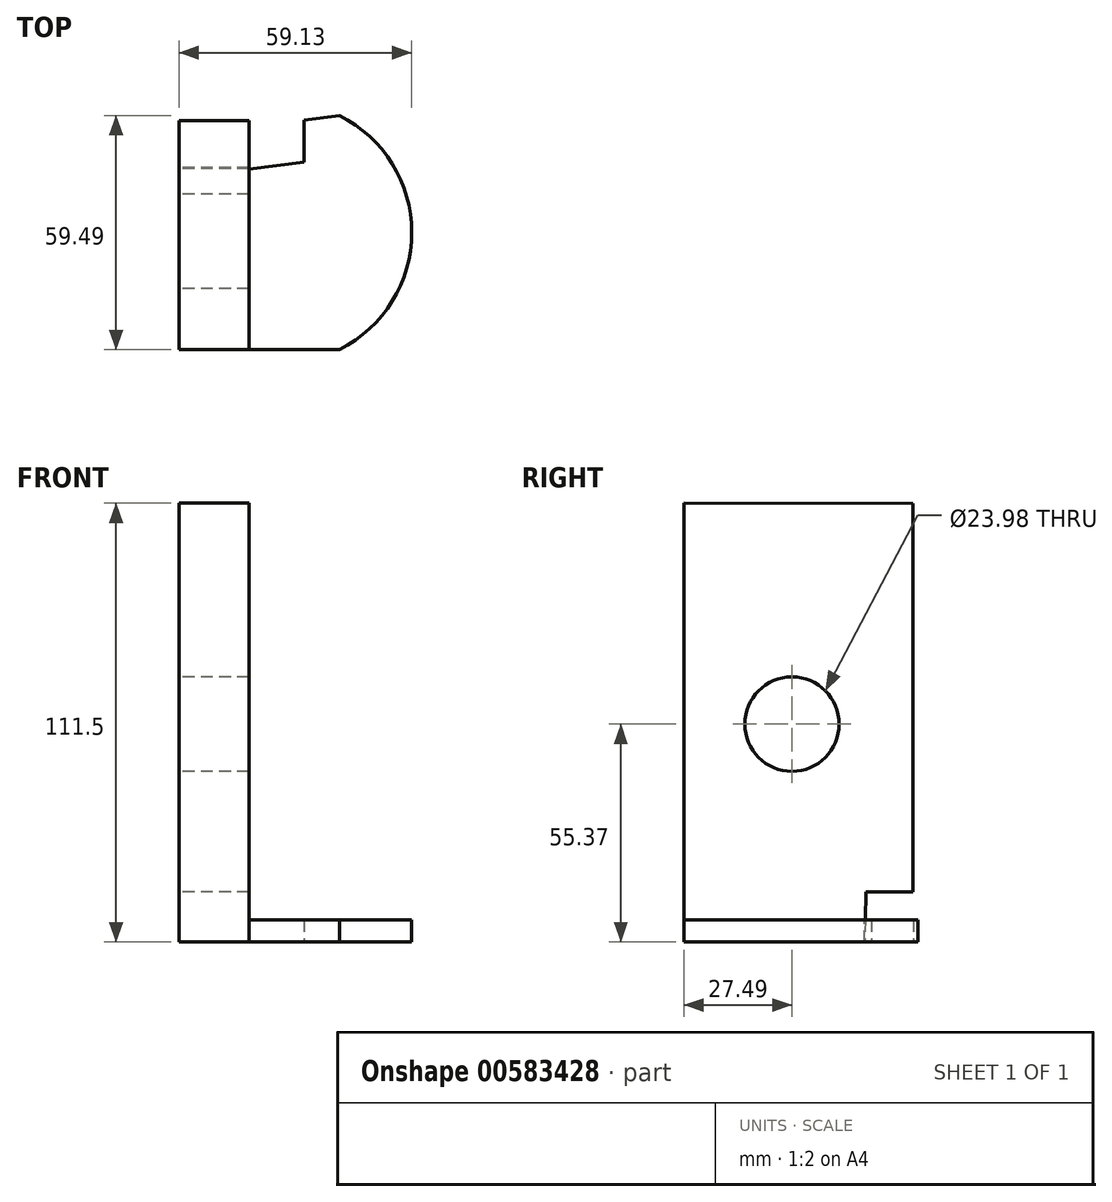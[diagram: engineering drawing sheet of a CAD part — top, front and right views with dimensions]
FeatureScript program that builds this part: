
annotation { "Feature Type Name" : "Feature", "Feature Type Description" : "" }
export const myFeature = defineFeature(function(context is Context, id is Id, definition is map)
    precondition{}
    {
        {
            var Q0;
            Q0=qCreatedBy(makeId("Right.planeOp"),FACE);
            var sketch = newSketch(context, id + "F0", { "sketchPlane" : qUnion([Q0])});
            skLineSegment(sketch, "E0.bottom", {"start": v(-27.5, 56.13) * mm, "end": v(30.67, 56.08) * mm});
            skLineSegment(sketch, "E0.left", {"start": v(-27.5, 56.13) * mm, "end": v(-27.5, -55.37) * mm});
            skCircle(sketch, "E1", {"center": v(0, 0) * mm, "radius": 11.99 * mm});
            skLineSegment(sketch, "E2", {"start": v(-11.99, 0) * mm, "end": v(-11.93, 56.12) * mm});
            skLineSegment(sketch, "E3", {"start": v(11.99, 0) * mm, "end": v(11.99, 56.1) * mm});
            skLineSegment(sketch, "E4", {"start": v(-27.5, -55.37) * mm, "end": v(18.47, -55.37) * mm});
            skLineSegment(sketch, "E5", {"start": v(18.84, -42.62) * mm, "end": v(30.67, -42.63) * mm});
            skLineSegment(sketch, "E6", {"start": v(18.84, -42.62) * mm, "end": v(18.47, -55.37) * mm});
            skPoint(sketch, "E7.startSnap0", {"position": v(24.75, -42.63) * mm});
            skLineSegment(sketch, "E8", {"start": v(30.67, 56.08) * mm, "end": v(30.67, -42.63) * mm});
            skSolve(sketch);
        }
        {
            var Q0;
            {var subQ4=sQuery(id+"F0.wireOp",EDGE,"E0.left");Q0=makeQuery(id+"F0.imprint","IMPRINT",FACE,{"disambiguationData":[TD([[makeQuery(id+"F0.imprint","IMPRINT",EDGE,{"derivedFrom":subQ4}),1.0]])]});}
            var Q1;
            {var subQ0=sQuery(id+"F0.wireOp",EDGE,"E2");Q1=makeQuery(id+"F0.imprint","IMPRINT",FACE,{"disambiguationData":[TD([[makeQuery(id+"F0.imprint","IMPRINT",EDGE,{"derivedFrom":subQ0}),-1.0]])]});}
            var Q2;
            {var subQ0=sQuery(id+"F0.wireOp",EDGE,"E1");var subQ3=makeQuery(id+"F0.imprint","IMPRINT",VERTEX,{"derivedFrom":subQ0});Q2=makeQuery(id+"F0.imprint","IMPRINT",FACE,{"disambiguationData":[TD([[makeQuery(id+"F0.imprint","IMPRINT",EDGE,{"disambiguationData":[TD([[subQ3,1.0]])],"derivedFrom":subQ0}),1.0]])]});}
            extrude(context, id + "F1", {"entities" : qUnion([Q0, Q1, Q2]), "depth" : 17.78 * mm, "offsetDistance" : 25.4 * mm});
        }
        {
            var Q0;
            Q0=makeQuery(id+"F1.opExtrude","CAP_FACE",FACE,{"disambiguationData":[OSD([sQuery(id+"F0.wireOp",EDGE,"E0.bottom"),sQuery(id+"F0.wireOp",EDGE,"E0.left"),sQuery(id+"F0.wireOp",EDGE,"E4"),sQuery(id+"F0.wireOp",EDGE,"E5"),sQuery(id+"F0.wireOp",EDGE,"E6"),sQuery(id+"F0.wireOp",EDGE,"E8")])],"isStart":false});
            var sketch = newSketch(context, id + "F2", { "sketchPlane" : qUnion([Q0])});
            skCircle(sketch, "E9", {"center": v(0, 0) * mm, "radius": 9.8 * mm});
            skLineSegment(sketch, "E10", {"start": v(-9.8, 0) * mm, "end": v(-7.53, 56.11) * mm});
            skLineSegment(sketch, "E11", {"start": v(9.8, 0) * mm, "end": v(9.85, 56.13) * mm});
            skSolve(sketch);
        }
        {
            var Q0;
            {var subQ0=sQuery(id+"F2.wireOp",EDGE,"E9");var subQ1=makeQuery(id+"F2.imprint","INTERSECT",VERTEX,{"derivedFrom":[subQ0,sQuery(id+"F2.wireOp",EDGE,"E11")]});Q0=makeQuery(id+"F2.imprint","IMPRINT",FACE,{"disambiguationData":[TD([[makeQuery(id+"F2.imprint","IMPRINT",EDGE,{"disambiguationData":[TD([[subQ1,-1.0]])],"derivedFrom":subQ0}),1.0]])]});}
            var Q1;
            {var subQ0=sQuery(id+"F2.wireOp",EDGE,"E11");var subQ1=sQuery(id+"F2.wireOp",EDGE,"E9");var subQ2=makeQuery(id+"F2.imprint","INTERSECT",VERTEX,{"derivedFrom":[subQ1,subQ0]});Q1=makeQuery(id+"F2.imprint","IMPRINT",FACE,{"disambiguationData":[TD([[makeQuery(id+"F2.imprint","IMPRINT",EDGE,{"disambiguationData":[TD([[subQ2,-1.0]])],"derivedFrom":subQ1}),-1.0]])]});}
            extrude(context, id + "F3", {"entities" : qUnion([Q0, Q1]), "operationType" : NewBodyOperationType.REMOVE, "oppositeDirection" : true, "depth" : 80.52 * mm, "offsetDistance" : 25.4 * mm});
        }
        {
            var Q0;
            Q0=makeQuery(id+"F1.opExtrude","SWEPT_FACE",FACE,{"disambiguationData":[OSD([sQuery(id+"F0.wireOp",EDGE,"E4")])]});
            cPlane(context, id + "F4", {"entities" : qUnion([Q0]), "cplaneType" : CPlaneType.OFFSET, "offset" : 0 * mm, "oppositeDirection" : true, "width" : 152.4 * mm, "height" : 152.4 * mm});
        }
        {
            var Q0;
            Q0=qCreatedBy(id+"F4.planeOp",FACE);
            var sketch = newSketch(context, id + "F5", { "sketchPlane" : qUnion([Q0])});
            skLineSegment(sketch, "E12", {"start": v(17.7, 27.44) * mm, "end": v(17.7, -18.43) * mm});
            skLineSegment(sketch, "E13", {"start": v(17.7, 27.44) * mm, "end": v(31.72, 27.44) * mm});
            skLineSegment(sketch, "E14", {"start": v(17.7, -18.43) * mm, "end": v(31.72, -20.23) * mm});
            skLineSegment(sketch, "E15", {"start": v(31.72, -19.1) * mm, "end": v(31.72, -30.84) * mm});
            skLineSegment(sketch, "E16", {"start": v(31.72, 27.44) * mm, "end": v(40.83, 27.44) * mm});
            skLineSegment(sketch, "E17", {"start": v(31.72, -30.84) * mm, "end": v(40.83, -32) * mm});
            skArc(sketch, "E18", {"start": v(40.83, -32) * mm, "mid": v(59.13, -2.28) * mm, "end": v(40.83, 27.44) * mm});
            skSolve(sketch);
        }
        {
            var Q0;
            Q0=makeQuery(id+"F5.imprint","IMPRINT",FACE,{"disambiguationData":[TD([[makeQuery(id+"F5.imprint","IMPRINT",EDGE,{"derivedFrom":sQuery(id+"F5.wireOp",EDGE,"E12")}),1.0]])]});
            extrude(context, id + "F6", {"entities" : qUnion([Q0]), "operationType" : NewBodyOperationType.ADD, "oppositeDirection" : true, "depth" : 5.6 * mm, "offsetDistance" : 25.4 * mm});
        }
    });
